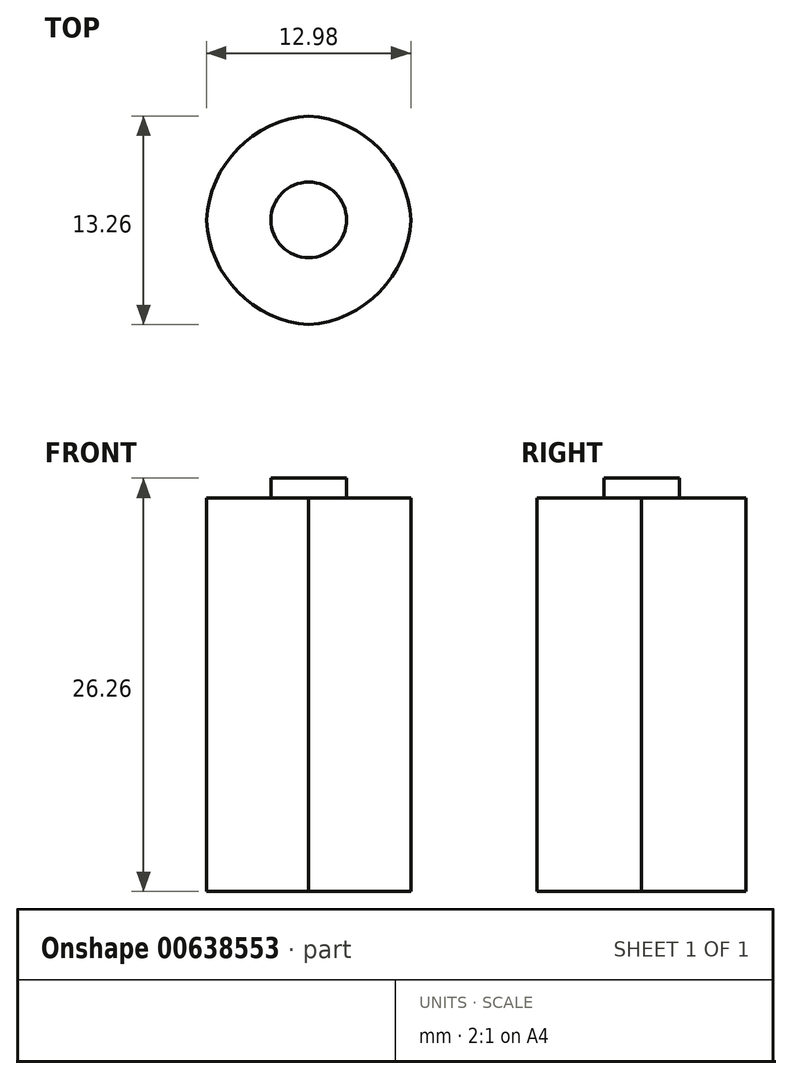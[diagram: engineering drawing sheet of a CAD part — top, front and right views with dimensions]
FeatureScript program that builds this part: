
annotation { "Feature Type Name" : "Feature", "Feature Type Description" : "" }
export const myFeature = defineFeature(function(context is Context, id is Id, definition is map)
    precondition{}
    {
        {
            var Q0;
            Q0=qCreatedBy(makeId("Front.planeOp"),FACE);
            var sketch = newSketch(context, id + "F0", { "sketchPlane" : qUnion([Q0])});
            skLineSegment(sketch, "E0.bottom", {"start": v(6.5, -14.06) * mm, "end": v(-6.5, -14.06) * mm});
            skLineSegment(sketch, "E0.top", {"start": v(6.5, 10.94) * mm, "end": v(-6.5, 10.94) * mm});
            skLineSegment(sketch, "E0.left", {"start": v(6.5, -14.06) * mm, "end": v(6.5, 10.94) * mm});
            skLineSegment(sketch, "E0.right", {"start": v(-6.5, -14.06) * mm, "end": v(-6.5, 10.94) * mm});
            skPoint(sketch, "E0.middle", {"position": v(0, -1.56) * mm});
            skSolve(sketch);
        }
        {
            var Q0;
            Q0 = qSketchRegion(id + "FfxP5vggtV829Ji_0", true);
            var Q1;
            Q1=makeQuery(id+"F0.imprint","IMPRINT",FACE,{"disambiguationData":[TD([[makeQuery(id+"F0.imprint","IMPRINT",EDGE,{"derivedFrom":sQuery(id+"F0.wireOp",EDGE,"E0.bottom")}),-1.0]])]});
            extrude(context, id + "F1", {"entities" : qUnion([Q0, Q1]), "depth" : 13.3 * mm, "offsetDistance" : 25 * mm});
        }
        {
            var Q0;
            Q0=makeQuery(id+"F1.opExtrude","CAP_EDGE",EDGE,{"disambiguationData":[OSD([sQuery(id+"F0.wireOp",EDGE,"E0.left")])],"isStart":false});
            var Q1;
            Q1=makeQuery(id+"F1.opExtrude","CAP_EDGE",EDGE,{"disambiguationData":[OSD([sQuery(id+"F0.wireOp",EDGE,"E0.left")])],"isStart":true});
            var Q2;
            Q2=makeQuery(id+"F1.opExtrude","CAP_EDGE",EDGE,{"disambiguationData":[OSD([sQuery(id+"F0.wireOp",EDGE,"E0.right")])],"isStart":true});
            var Q3;
            Q3=makeQuery(id+"F1.opExtrude","CAP_EDGE",EDGE,{"disambiguationData":[OSD([sQuery(id+"F0.wireOp",EDGE,"E0.right")])],"isStart":false});
            fillet(context, id + "F2", {"entities" : qUnion([Q0, Q1, Q2, Q3]), "radius" : 7 * mm, "tangentPropagation" : true, "allowEdgeOverflow" : false});
        }
        {
            var Q0;
            Q0=qCreatedBy(makeId("Top.planeOp"),FACE);
            var sketch = newSketch(context, id + "F3", { "sketchPlane" : qUnion([Q0])});
            skCircle(sketch, "E1", {"center": v(0, -6.62) * mm, "radius": 2.4 * mm});
            skSolve(sketch);
        }
        {
            var Q0;
            Q0 = qSketchRegion(id + "F3", true);
            extrude(context, id + "F4", {"entities" : qUnion([Q0]), "operationType" : NewBodyOperationType.ADD, "depth" : 12.2 * mm, "offsetDistance" : 25 * mm});
        }
    });
